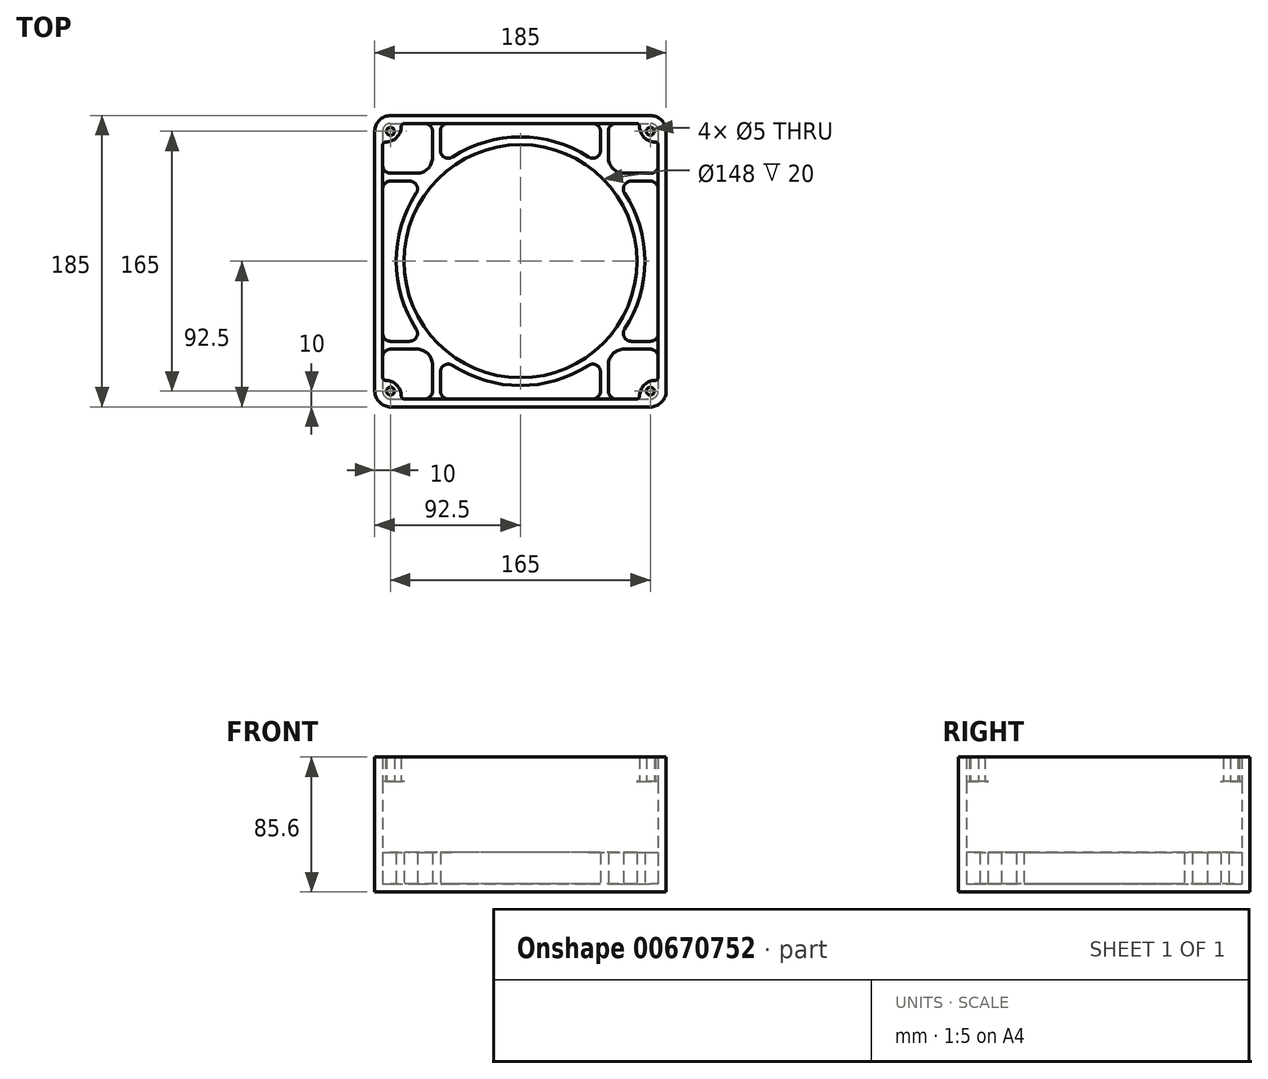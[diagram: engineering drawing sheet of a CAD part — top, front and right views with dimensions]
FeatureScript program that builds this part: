
annotation { "Feature Type Name" : "Feature", "Feature Type Description" : "" }
export const myFeature = defineFeature(function(context is Context, id is Id, definition is map)
    precondition{}
    {
        {
            var Q0;
            Q0=qCreatedBy(makeId("Top.planeOp"),FACE);
            var sketch = newSketch(context, id + "F0", { "sketchPlane" : qUnion([Q0])});
            skLineSegment(sketch, "E0.bottom", {"start": v(-82.5, 92.5) * mm, "end": v(82.5, 92.5) * mm});
            skLineSegment(sketch, "E0.top", {"start": v(-82.5, -92.5) * mm, "end": v(82.5, -92.5) * mm});
            skLineSegment(sketch, "E0.left", {"start": v(-92.5, 82.5) * mm, "end": v(-92.5, -82.5) * mm});
            skLineSegment(sketch, "E0.right", {"start": v(92.5, 82.5) * mm, "end": v(92.5, -82.5) * mm});
            skLineSegment(sketch, "E1", {"start": v(-92.5, 92.5) * mm, "end": v(92.5, -92.5) * mm, "construction": true});
            skLineSegment(sketch, "E2", {"start": v(-92.5, -92.5) * mm, "end": v(92.5, 92.5) * mm, "construction": true});
            skCircle(sketch, "E3", {"center": v(0, 0) * mm, "radius": 74 * mm});
            skArc(sketch, "E4.0", {"start": v(-66.19, 43.13) * mm, "mid": v(-79, 0) * mm, "end": v(-66.19, -43.13) * mm});
            skPoint(sketch, "E5.visualSharp", {"position": v(-92.5, 92.5) * mm});
            skArc(sketch, "E5.filletArc", {"start": v(-82.5, 92.5) * mm, "mid": v(-89.57, 89.57) * mm, "end": v(-92.5, 82.5) * mm});
            skPoint(sketch, "E6.visualSharp", {"position": v(92.5, 92.5) * mm});
            skArc(sketch, "E6.filletArc", {"start": v(92.5, 82.5) * mm, "mid": v(89.57, 89.57) * mm, "end": v(82.5, 92.5) * mm});
            skPoint(sketch, "E7.visualSharp", {"position": v(92.5, -92.5) * mm});
            skArc(sketch, "E7.filletArc", {"start": v(82.5, -92.5) * mm, "mid": v(89.57, -89.57) * mm, "end": v(92.5, -82.5) * mm});
            skPoint(sketch, "E8.visualSharp", {"position": v(-92.5, -92.5) * mm});
            skArc(sketch, "E8.filletArc", {"start": v(-92.5, -82.5) * mm, "mid": v(-89.57, -89.57) * mm, "end": v(-82.5, -92.5) * mm});
            skArc(sketch, "E9.0", {"start": v(-82.5, 87.5) * mm, "mid": v(-86.04, 86.04) * mm, "end": v(-87.5, 82.5) * mm});
            skLineSegment(sketch, "E9.1", {"start": v(-82.5, 87.5) * mm, "end": v(-60.86, 87.5) * mm});
            skLineSegment(sketch, "E9.2", {"start": v(-87.5, 82.5) * mm, "end": v(-87.5, 60.86) * mm});
            skArc(sketch, "E9.3", {"start": v(87.5, 82.5) * mm, "mid": v(86.04, 86.04) * mm, "end": v(82.5, 87.5) * mm});
            skArc(sketch, "E9.4", {"start": v(-87.5, -82.5) * mm, "mid": v(-86.04, -86.04) * mm, "end": v(-82.5, -87.5) * mm});
            skLineSegment(sketch, "E9.5", {"start": v(-82.5, -87.5) * mm, "end": v(-60.86, -87.5) * mm});
            skArc(sketch, "E9.6", {"start": v(82.5, -87.5) * mm, "mid": v(86.04, -86.04) * mm, "end": v(87.5, -82.5) * mm});
            skLineSegment(sketch, "E9.7", {"start": v(87.5, 82.5) * mm, "end": v(87.5, 60.86) * mm});
            skLineSegment(sketch, "E10", {"start": v(-55.86, 65.86) * mm, "end": v(-55.86, 82.5) * mm});
            skLineSegment(sketch, "E11", {"start": v(-65.86, 55.86) * mm, "end": v(-82.5, 55.86) * mm});
            skLineSegment(sketch, "E12", {"start": v(-50.86, 82.5) * mm, "end": v(-50.86, 70.38) * mm});
            skLineSegment(sketch, "E13", {"start": v(-82.5, 50.86) * mm, "end": v(-70.38, 50.86) * mm});
            skLineSegment(sketch, "E14", {"start": v(55.86, 65.86) * mm, "end": v(55.86, 82.5) * mm});
            skLineSegment(sketch, "E15", {"start": v(65.86, 55.86) * mm, "end": v(82.5, 55.86) * mm});
            skLineSegment(sketch, "E16", {"start": v(50.86, 82.5) * mm, "end": v(50.86, 70.38) * mm});
            skLineSegment(sketch, "E17", {"start": v(70.38, 50.86) * mm, "end": v(82.5, 50.86) * mm});
            skLineSegment(sketch, "E18", {"start": v(65.86, -55.86) * mm, "end": v(82.5, -55.86) * mm});
            skLineSegment(sketch, "E19", {"start": v(55.86, -65.86) * mm, "end": v(55.86, -82.5) * mm});
            skLineSegment(sketch, "E20", {"start": v(70.38, -50.86) * mm, "end": v(82.5, -50.86) * mm});
            skLineSegment(sketch, "E21", {"start": v(50.86, -70.38) * mm, "end": v(50.86, -82.5) * mm});
            skLineSegment(sketch, "E22", {"start": v(-55.86, -65.86) * mm, "end": v(-55.86, -82.5) * mm});
            skLineSegment(sketch, "E23", {"start": v(-65.86, -55.86) * mm, "end": v(-82.5, -55.86) * mm});
            skLineSegment(sketch, "E24", {"start": v(-50.86, -82.5) * mm, "end": v(-50.86, -70.38) * mm});
            skLineSegment(sketch, "E25", {"start": v(-82.5, -50.86) * mm, "end": v(-70.38, -50.86) * mm});
            skPoint(sketch, "E26.visualSharp", {"position": v(-55.86, 55.86) * mm});
            skArc(sketch, "E26.filletArc", {"start": v(-65.86, 55.86) * mm, "mid": v(-58.8, 58.8) * mm, "end": v(-55.86, 65.86) * mm});
            skPoint(sketch, "E27.visualSharp", {"position": v(55.86, 55.86) * mm});
            skArc(sketch, "E27.filletArc", {"start": v(55.86, 65.86) * mm, "mid": v(58.8, 58.8) * mm, "end": v(65.86, 55.86) * mm});
            skPoint(sketch, "E28.visualSharp", {"position": v(55.86, -55.86) * mm});
            skArc(sketch, "E28.filletArc", {"start": v(65.86, -55.86) * mm, "mid": v(58.8, -58.8) * mm, "end": v(55.86, -65.86) * mm});
            skPoint(sketch, "E29.visualSharp", {"position": v(-55.86, -55.86) * mm});
            skArc(sketch, "E29.filletArc", {"start": v(-55.86, -65.86) * mm, "mid": v(-58.8, -58.8) * mm, "end": v(-65.86, -55.86) * mm});
            skLineSegment(sketch, "E30.trimOffspring", {"start": v(-87.5, 45.86) * mm, "end": v(-87.5, -45.86) * mm});
            skLineSegment(sketch, "E31.trimOffspring", {"start": v(-45.86, 87.5) * mm, "end": v(45.86, 87.5) * mm});
            skArc(sketch, "E32.trimOffspring", {"start": v(43.13, 66.19) * mm, "mid": v(0, 79) * mm, "end": v(-43.13, 66.19) * mm});
            skLineSegment(sketch, "E33.trimOffspring", {"start": v(60.86, 87.5) * mm, "end": v(82.5, 87.5) * mm});
            skLineSegment(sketch, "E34.trimOffspring", {"start": v(87.5, 45.86) * mm, "end": v(87.5, -45.86) * mm});
            skLineSegment(sketch, "E35.trimOffspring", {"start": v(87.5, -60.86) * mm, "end": v(87.5, -82.5) * mm});
            skArc(sketch, "E36.trimOffspring", {"start": v(66.19, -43.13) * mm, "mid": v(79, 0) * mm, "end": v(66.19, 43.13) * mm});
            skLineSegment(sketch, "E37.trimOffspring", {"start": v(60.86, -87.5) * mm, "end": v(82.5, -87.5) * mm});
            skLineSegment(sketch, "E38.trimOffspring", {"start": v(-45.86, -87.5) * mm, "end": v(45.86, -87.5) * mm});
            skLineSegment(sketch, "E39.trimOffspring", {"start": v(-87.5, -60.86) * mm, "end": v(-87.5, -82.5) * mm});
            skArc(sketch, "E40.trimOffspring", {"start": v(-43.13, -66.19) * mm, "mid": v(0, -79) * mm, "end": v(43.13, -66.19) * mm});
            skPoint(sketch, "E41.visualSharp", {"position": v(-55.86, 87.5) * mm});
            skArc(sketch, "E41.filletArc", {"start": v(-55.86, 82.5) * mm, "mid": v(-57.33, 86.04) * mm, "end": v(-60.86, 87.5) * mm});
            skPoint(sketch, "E42.visualSharp", {"position": v(-50.86, 87.5) * mm});
            skArc(sketch, "E42.filletArc", {"start": v(-45.86, 87.5) * mm, "mid": v(-49.4, 86.04) * mm, "end": v(-50.86, 82.5) * mm});
            skPoint(sketch, "E43.visualSharp", {"position": v(-50.86, 60.45) * mm});
            skArc(sketch, "E43.filletArc", {"start": v(-50.86, 70.38) * mm, "mid": v(-48.24, 65.98) * mm, "end": v(-43.13, 66.19) * mm});
            skPoint(sketch, "E44.visualSharp", {"position": v(-60.45, 50.86) * mm});
            skArc(sketch, "E44.filletArc", {"start": v(-66.19, 43.13) * mm, "mid": v(-65.98, 48.24) * mm, "end": v(-70.38, 50.86) * mm});
            skPoint(sketch, "E45.visualSharp", {"position": v(-87.5, 50.86) * mm});
            skArc(sketch, "E45.filletArc", {"start": v(-82.5, 50.86) * mm, "mid": v(-86.04, 49.4) * mm, "end": v(-87.5, 45.86) * mm});
            skPoint(sketch, "E46.visualSharp", {"position": v(-87.5, 55.86) * mm});
            skArc(sketch, "E46.filletArc", {"start": v(-87.5, 60.86) * mm, "mid": v(-86.04, 57.33) * mm, "end": v(-82.5, 55.86) * mm});
            skPoint(sketch, "E47.visualSharp", {"position": v(55.86, 87.5) * mm});
            skArc(sketch, "E47.filletArc", {"start": v(60.86, 87.5) * mm, "mid": v(57.33, 86.04) * mm, "end": v(55.86, 82.5) * mm});
            skPoint(sketch, "E48.visualSharp", {"position": v(50.86, 87.5) * mm});
            skArc(sketch, "E48.filletArc", {"start": v(50.86, 82.5) * mm, "mid": v(49.4, 86.04) * mm, "end": v(45.86, 87.5) * mm});
            skPoint(sketch, "E49.visualSharp", {"position": v(50.86, 60.45) * mm});
            skArc(sketch, "E49.filletArc", {"start": v(43.13, 66.19) * mm, "mid": v(48.24, 65.98) * mm, "end": v(50.86, 70.38) * mm});
            skPoint(sketch, "E50.visualSharp", {"position": v(60.45, 50.86) * mm});
            skArc(sketch, "E50.filletArc", {"start": v(70.38, 50.86) * mm, "mid": v(65.98, 48.24) * mm, "end": v(66.19, 43.13) * mm});
            skPoint(sketch, "E51.visualSharp", {"position": v(87.5, 55.86) * mm});
            skArc(sketch, "E51.filletArc", {"start": v(82.5, 55.86) * mm, "mid": v(86.04, 57.33) * mm, "end": v(87.5, 60.86) * mm});
            skPoint(sketch, "E52.visualSharp", {"position": v(87.5, 50.86) * mm});
            skArc(sketch, "E52.filletArc", {"start": v(87.5, 45.86) * mm, "mid": v(86.04, 49.4) * mm, "end": v(82.5, 50.86) * mm});
            skPoint(sketch, "E53.visualSharp", {"position": v(87.5, -50.86) * mm});
            skArc(sketch, "E53.filletArc", {"start": v(82.5, -50.86) * mm, "mid": v(86.04, -49.4) * mm, "end": v(87.5, -45.86) * mm});
            skPoint(sketch, "E54.visualSharp", {"position": v(87.5, -55.86) * mm});
            skArc(sketch, "E54.filletArc", {"start": v(87.5, -60.86) * mm, "mid": v(86.04, -57.33) * mm, "end": v(82.5, -55.86) * mm});
            skPoint(sketch, "E55.visualSharp", {"position": v(60.45, -50.86) * mm});
            skArc(sketch, "E55.filletArc", {"start": v(66.19, -43.13) * mm, "mid": v(65.98, -48.24) * mm, "end": v(70.38, -50.86) * mm});
            skPoint(sketch, "E56.visualSharp", {"position": v(50.86, -60.45) * mm});
            skArc(sketch, "E56.filletArc", {"start": v(50.86, -70.38) * mm, "mid": v(48.24, -65.98) * mm, "end": v(43.13, -66.19) * mm});
            skPoint(sketch, "E57.visualSharp", {"position": v(55.86, -87.5) * mm});
            skArc(sketch, "E57.filletArc", {"start": v(55.86, -82.5) * mm, "mid": v(57.33, -86.04) * mm, "end": v(60.86, -87.5) * mm});
            skPoint(sketch, "E58.visualSharp", {"position": v(50.86, -87.5) * mm});
            skArc(sketch, "E58.filletArc", {"start": v(45.86, -87.5) * mm, "mid": v(49.4, -86.04) * mm, "end": v(50.86, -82.5) * mm});
            skPoint(sketch, "E59.visualSharp", {"position": v(-55.86, -87.5) * mm});
            skArc(sketch, "E59.filletArc", {"start": v(-60.86, -87.5) * mm, "mid": v(-57.33, -86.04) * mm, "end": v(-55.86, -82.5) * mm});
            skPoint(sketch, "E60.visualSharp", {"position": v(-50.86, -87.5) * mm});
            skArc(sketch, "E60.filletArc", {"start": v(-50.86, -82.5) * mm, "mid": v(-49.4, -86.04) * mm, "end": v(-45.86, -87.5) * mm});
            skPoint(sketch, "E61.visualSharp", {"position": v(-50.86, -60.45) * mm});
            skArc(sketch, "E61.filletArc", {"start": v(-43.13, -66.19) * mm, "mid": v(-48.24, -65.98) * mm, "end": v(-50.86, -70.38) * mm});
            skPoint(sketch, "E62.visualSharp", {"position": v(-60.45, -50.86) * mm});
            skArc(sketch, "E62.filletArc", {"start": v(-70.38, -50.86) * mm, "mid": v(-65.98, -48.24) * mm, "end": v(-66.19, -43.13) * mm});
            skPoint(sketch, "E63.visualSharp", {"position": v(-87.5, -50.86) * mm});
            skArc(sketch, "E63.filletArc", {"start": v(-87.5, -45.86) * mm, "mid": v(-86.04, -49.4) * mm, "end": v(-82.5, -50.86) * mm});
            skPoint(sketch, "E64.visualSharp", {"position": v(-87.5, -55.86) * mm});
            skArc(sketch, "E64.filletArc", {"start": v(-82.5, -55.86) * mm, "mid": v(-86.04, -57.33) * mm, "end": v(-87.5, -60.86) * mm});
            skSolve(sketch);
        }
        {
            var Q0;
            Q0=makeQuery(id+"F0.imprint","IMPRINT",FACE,{"disambiguationData":[TD([[makeQuery(id+"F0.imprint","IMPRINT",EDGE,{"derivedFrom":sQuery(id+"F0.wireOp",EDGE,"E0.bottom")}),-1.0]])]});
            var Q1;
            Q1=makeQuery(id+"F0.imprint","IMPRINT",FACE,{"disambiguationData":[TD([[makeQuery(id+"F0.imprint","IMPRINT",EDGE,{"derivedFrom":sQuery(id+"F0.wireOp",EDGE,"E3")}),1.0]])]});
            var Q2;
            Q2=makeQuery(id+"F0.imprint","IMPRINT",FACE,{"disambiguationData":[TD([[makeQuery(id+"F0.imprint","IMPRINT",EDGE,{"derivedFrom":sQuery(id+"F0.wireOp",EDGE,"E3")}),-1.0]])]});
            var Q3;
            {var subQ5=sQuery(id+"F0.wireOp",EDGE,"E9.0");Q3=makeQuery(id+"F0.imprint","IMPRINT",FACE,{"disambiguationData":[TD([[makeQuery(id+"F0.imprint","IMPRINT",EDGE,{"derivedFrom":subQ5}),1.0]])]});}
            var Q4;
            {var subQ5=sQuery(id+"F0.wireOp",EDGE,"E9.4");Q4=makeQuery(id+"F0.imprint","IMPRINT",FACE,{"disambiguationData":[TD([[makeQuery(id+"F0.imprint","IMPRINT",EDGE,{"derivedFrom":subQ5}),1.0]])]});}
            var Q5;
            {var subQ5=sQuery(id+"F0.wireOp",EDGE,"E9.6");Q5=makeQuery(id+"F0.imprint","IMPRINT",FACE,{"disambiguationData":[TD([[makeQuery(id+"F0.imprint","IMPRINT",EDGE,{"derivedFrom":subQ5}),1.0]])]});}
            var Q6;
            {var subQ5=sQuery(id+"F0.wireOp",EDGE,"E9.3");Q6=makeQuery(id+"F0.imprint","IMPRINT",FACE,{"disambiguationData":[TD([[makeQuery(id+"F0.imprint","IMPRINT",EDGE,{"derivedFrom":subQ5}),1.0]])]});}
            var Q7;
            Q7=makeQuery(id+"F0.imprint","IMPRINT",FACE,{"disambiguationData":[TD([[makeQuery(id+"F0.imprint","IMPRINT",EDGE,{"derivedFrom":sQuery(id+"F0.wireOp",EDGE,"E4.0")}),-1.0]])]});
            var Q8;
            Q8=makeQuery(id+"F0.imprint","IMPRINT",FACE,{"disambiguationData":[TD([[makeQuery(id+"F0.imprint","IMPRINT",EDGE,{"derivedFrom":sQuery(id+"F0.wireOp",EDGE,"E12")}),1.0]])]});
            var Q9;
            Q9=makeQuery(id+"F0.imprint","IMPRINT",FACE,{"disambiguationData":[TD([[makeQuery(id+"F0.imprint","IMPRINT",EDGE,{"derivedFrom":sQuery(id+"F0.wireOp",EDGE,"E21")}),-1.0]])]});
            var Q10;
            Q10=makeQuery(id+"F0.imprint","IMPRINT",FACE,{"disambiguationData":[TD([[makeQuery(id+"F0.imprint","IMPRINT",EDGE,{"derivedFrom":sQuery(id+"F0.wireOp",EDGE,"E17")}),-1.0]])]});
            extrude(context, id + "F1", {"entities" : qUnion([Q0, Q1, Q2, Q3, Q4, Q5, Q6, Q7, Q8, Q9, Q10]), "oppositeDirection" : true, "depth" : 5 * mm, "offsetDistance" : 25 * mm});
        }
        {
            var Q0;
            Q0 = qSketchRegion(id + "F0", true);
            extrude(context, id + "F2", {"entities" : qUnion([Q0]), "operationType" : NewBodyOperationType.ADD, "depth" : 20 * mm, "offsetDistance" : 25 * mm});
        }
        {
            var Q0;
            Q0=makeQuery(id+"F2.opExtrude","CAP_FACE",FACE,{"disambiguationData":[OSD([sQuery(id+"F0.wireOp",EDGE,"E0.bottom"),sQuery(id+"F0.wireOp",EDGE,"E0.top"),sQuery(id+"F0.wireOp",EDGE,"E0.left"),sQuery(id+"F0.wireOp",EDGE,"E0.right"),sQuery(id+"F0.wireOp",EDGE,"E3"),sQuery(id+"F0.wireOp",EDGE,"E4.0"),sQuery(id+"F0.wireOp",EDGE,"E5.filletArc"),sQuery(id+"F0.wireOp",EDGE,"E6.filletArc"),sQuery(id+"F0.wireOp",EDGE,"E7.filletArc"),sQuery(id+"F0.wireOp",EDGE,"E8.filletArc"),sQuery(id+"F0.wireOp",EDGE,"E9.0"),sQuery(id+"F0.wireOp",EDGE,"E9.1"),sQuery(id+"F0.wireOp",EDGE,"E9.2"),sQuery(id+"F0.wireOp",EDGE,"E9.3"),sQuery(id+"F0.wireOp",EDGE,"E9.4"),sQuery(id+"F0.wireOp",EDGE,"E9.5"),sQuery(id+"F0.wireOp",EDGE,"E9.6"),sQuery(id+"F0.wireOp",EDGE,"E9.7"),sQuery(id+"F0.wireOp",EDGE,"E10"),sQuery(id+"F0.wireOp",EDGE,"E11"),sQuery(id+"F0.wireOp",EDGE,"E12"),sQuery(id+"F0.wireOp",EDGE,"E13"),sQuery(id+"F0.wireOp",EDGE,"E14"),sQuery(id+"F0.wireOp",EDGE,"E15"),sQuery(id+"F0.wireOp",EDGE,"E16"),sQuery(id+"F0.wireOp",EDGE,"E17"),sQuery(id+"F0.wireOp",EDGE,"E18"),sQuery(id+"F0.wireOp",EDGE,"E19"),sQuery(id+"F0.wireOp",EDGE,"E20"),sQuery(id+"F0.wireOp",EDGE,"E21"),sQuery(id+"F0.wireOp",EDGE,"E22"),sQuery(id+"F0.wireOp",EDGE,"E23"),sQuery(id+"F0.wireOp",EDGE,"E24"),sQuery(id+"F0.wireOp",EDGE,"E25"),sQuery(id+"F0.wireOp",EDGE,"E26.filletArc"),sQuery(id+"F0.wireOp",EDGE,"E27.filletArc"),sQuery(id+"F0.wireOp",EDGE,"E28.filletArc"),sQuery(id+"F0.wireOp",EDGE,"E29.filletArc"),sQuery(id+"F0.wireOp",EDGE,"E30.trimOffspring"),sQuery(id+"F0.wireOp",EDGE,"E31.trimOffspring"),sQuery(id+"F0.wireOp",EDGE,"E32.trimOffspring"),sQuery(id+"F0.wireOp",EDGE,"E33.trimOffspring"),sQuery(id+"F0.wireOp",EDGE,"E34.trimOffspring"),sQuery(id+"F0.wireOp",EDGE,"E35.trimOffspring"),sQuery(id+"F0.wireOp",EDGE,"E36.trimOffspring"),sQuery(id+"F0.wireOp",EDGE,"E37.trimOffspring"),sQuery(id+"F0.wireOp",EDGE,"E38.trimOffspring"),sQuery(id+"F0.wireOp",EDGE,"E39.trimOffspring"),sQuery(id+"F0.wireOp",EDGE,"E40.trimOffspring"),sQuery(id+"F0.wireOp",EDGE,"E41.filletArc"),sQuery(id+"F0.wireOp",EDGE,"E42.filletArc"),sQuery(id+"F0.wireOp",EDGE,"E43.filletArc"),sQuery(id+"F0.wireOp",EDGE,"E44.filletArc"),sQuery(id+"F0.wireOp",EDGE,"E45.filletArc"),sQuery(id+"F0.wireOp",EDGE,"E46.filletArc"),sQuery(id+"F0.wireOp",EDGE,"E47.filletArc"),sQuery(id+"F0.wireOp",EDGE,"E48.filletArc"),sQuery(id+"F0.wireOp",EDGE,"E49.filletArc"),sQuery(id+"F0.wireOp",EDGE,"E50.filletArc"),sQuery(id+"F0.wireOp",EDGE,"E51.filletArc"),sQuery(id+"F0.wireOp",EDGE,"E52.filletArc"),sQuery(id+"F0.wireOp",EDGE,"E53.filletArc"),sQuery(id+"F0.wireOp",EDGE,"E54.filletArc"),sQuery(id+"F0.wireOp",EDGE,"E55.filletArc"),sQuery(id+"F0.wireOp",EDGE,"E56.filletArc"),sQuery(id+"F0.wireOp",EDGE,"E57.filletArc"),sQuery(id+"F0.wireOp",EDGE,"E58.filletArc"),sQuery(id+"F0.wireOp",EDGE,"E59.filletArc"),sQuery(id+"F0.wireOp",EDGE,"E60.filletArc"),sQuery(id+"F0.wireOp",EDGE,"E61.filletArc"),sQuery(id+"F0.wireOp",EDGE,"E62.filletArc"),sQuery(id+"F0.wireOp",EDGE,"E63.filletArc"),sQuery(id+"F0.wireOp",EDGE,"E64.filletArc")])],"isStart":false});
            var sketch = newSketch(context, id + "F3", { "sketchPlane" : qUnion([Q0])});
            skLineSegment(sketch, "E65.0", {"start": v(-92.5, 82.5) * mm, "end": v(-92.5, -82.5) * mm});
            skArc(sketch, "E65.1", {"start": v(-82.5, 92.5) * mm, "mid": v(-89.57, 89.57) * mm, "end": v(-92.5, 82.5) * mm});
            skLineSegment(sketch, "E65.2", {"start": v(-82.5, 92.5) * mm, "end": v(82.5, 92.5) * mm});
            skArc(sketch, "E65.3", {"start": v(92.5, 82.5) * mm, "mid": v(89.57, 89.57) * mm, "end": v(82.5, 92.5) * mm});
            skLineSegment(sketch, "E65.4", {"start": v(92.5, 82.5) * mm, "end": v(92.5, -82.5) * mm});
            skArc(sketch, "E65.5", {"start": v(82.5, -92.5) * mm, "mid": v(89.57, -89.57) * mm, "end": v(92.5, -82.5) * mm});
            skLineSegment(sketch, "E65.6", {"start": v(-82.5, -92.5) * mm, "end": v(82.5, -92.5) * mm});
            skArc(sketch, "E65.7", {"start": v(-92.5, -82.5) * mm, "mid": v(-89.57, -89.57) * mm, "end": v(-82.5, -92.5) * mm});
            skArc(sketch, "E66.0", {"start": v(-82.5, 87.5) * mm, "mid": v(-86.04, 86.04) * mm, "end": v(-87.5, 82.5) * mm});
            skLineSegment(sketch, "E66.1", {"start": v(-82.5, 87.5) * mm, "end": v(82.5, 87.5) * mm});
            skLineSegment(sketch, "E66.2", {"start": v(-87.5, 82.5) * mm, "end": v(-87.5, -82.5) * mm});
            skArc(sketch, "E66.3", {"start": v(87.5, 82.5) * mm, "mid": v(86.04, 86.04) * mm, "end": v(82.5, 87.5) * mm});
            skArc(sketch, "E66.4", {"start": v(-87.5, -82.5) * mm, "mid": v(-86.04, -86.04) * mm, "end": v(-82.5, -87.5) * mm});
            skLineSegment(sketch, "E66.5", {"start": v(-82.5, -87.5) * mm, "end": v(82.5, -87.5) * mm});
            skArc(sketch, "E66.6", {"start": v(82.5, -87.5) * mm, "mid": v(86.04, -86.04) * mm, "end": v(87.5, -82.5) * mm});
            skLineSegment(sketch, "E66.7", {"start": v(87.5, 82.5) * mm, "end": v(87.5, -82.5) * mm});
            skSolve(sketch);
        }
        {
            var Q0;
            Q0 = qSketchRegion(id + "F3", true);
            extrude(context, id + "F4", {"entities" : qUnion([Q0]), "operationType" : NewBodyOperationType.ADD, "depth" : (65.1 - 20) * mm, "offsetDistance" : 25 * mm});
        }
        {
            var Q0;
            Q0=makeQuery(id+"F4.opExtrude","CAP_FACE",FACE,{"disambiguationData":[OSD([sQuery(id+"F3.wireOp",EDGE,"E65.0"),sQuery(id+"F3.wireOp",EDGE,"E65.1"),sQuery(id+"F3.wireOp",EDGE,"E65.2"),sQuery(id+"F3.wireOp",EDGE,"E65.3"),sQuery(id+"F3.wireOp",EDGE,"E65.4"),sQuery(id+"F3.wireOp",EDGE,"E65.5"),sQuery(id+"F3.wireOp",EDGE,"E65.6"),sQuery(id+"F3.wireOp",EDGE,"E65.7"),sQuery(id+"F3.wireOp",EDGE,"E66.0"),sQuery(id+"F3.wireOp",EDGE,"E66.1"),sQuery(id+"F3.wireOp",EDGE,"E66.2"),sQuery(id+"F3.wireOp",EDGE,"E66.3"),sQuery(id+"F3.wireOp",EDGE,"E66.4"),sQuery(id+"F3.wireOp",EDGE,"E66.5"),sQuery(id+"F3.wireOp",EDGE,"E66.6"),sQuery(id+"F3.wireOp",EDGE,"E66.7")])],"isStart":false});
            var sketch = newSketch(context, id + "F5", { "sketchPlane" : qUnion([Q0])});
            skArc(sketch, "E67.0", {"start": v(-82.5, 92.5) * mm, "mid": v(-89.57, 89.57) * mm, "end": v(-92.5, 82.5) * mm});
            skLineSegment(sketch, "E67.1", {"start": v(-82.5, 92.5) * mm, "end": v(82.5, 92.5) * mm});
            skLineSegment(sketch, "E67.2", {"start": v(-92.5, 82.5) * mm, "end": v(-92.5, -82.5) * mm});
            skArc(sketch, "E67.3", {"start": v(-92.5, -82.5) * mm, "mid": v(-89.57, -89.57) * mm, "end": v(-82.5, -92.5) * mm});
            skLineSegment(sketch, "E67.4", {"start": v(-82.5, -92.5) * mm, "end": v(82.5, -92.5) * mm});
            skArc(sketch, "E67.5", {"start": v(82.5, -92.5) * mm, "mid": v(89.57, -89.57) * mm, "end": v(92.5, -82.5) * mm});
            skLineSegment(sketch, "E67.6", {"start": v(92.5, 82.5) * mm, "end": v(92.5, -82.5) * mm});
            skArc(sketch, "E67.7", {"start": v(92.5, 82.5) * mm, "mid": v(89.57, 89.57) * mm, "end": v(82.5, 92.5) * mm});
            skLineSegment(sketch, "E68.1", {"start": v(-73.68, 87.5) * mm, "end": v(-60.86, 87.5) * mm});
            skLineSegment(sketch, "E68.2", {"start": v(-87.5, 73.68) * mm, "end": v(-87.5, 60.86) * mm});
            skLineSegment(sketch, "E68.5", {"start": v(-73.68, -87.5) * mm, "end": v(-60.86, -87.5) * mm});
            skLineSegment(sketch, "E68.7", {"start": v(87.5, 73.68) * mm, "end": v(87.5, 60.86) * mm});
            skLineSegment(sketch, "E69.trimOffspring", {"start": v(-45.86, 87.5) * mm, "end": v(45.86, 87.5) * mm});
            skLineSegment(sketch, "E70.trimOffspring", {"start": v(-87.5, 45.86) * mm, "end": v(-87.5, -45.86) * mm});
            skLineSegment(sketch, "E71.trimOffspring", {"start": v(60.86, 87.5) * mm, "end": v(73.68, 87.5) * mm});
            skLineSegment(sketch, "E72.trimOffspring", {"start": v(87.5, 45.86) * mm, "end": v(87.5, -45.86) * mm});
            skLineSegment(sketch, "E73.trimOffspring", {"start": v(87.5, -60.86) * mm, "end": v(87.5, -73.68) * mm});
            skLineSegment(sketch, "E74.trimOffspring", {"start": v(60.86, -87.5) * mm, "end": v(73.68, -87.5) * mm});
            skLineSegment(sketch, "E75.trimOffspring", {"start": v(-45.86, -87.5) * mm, "end": v(45.86, -87.5) * mm});
            skLineSegment(sketch, "E76.trimOffspring", {"start": v(-87.5, -60.86) * mm, "end": v(-87.5, -73.68) * mm});
            skLineSegment(sketch, "E77", {"start": v(75.68, 75.68) * mm, "end": v(89.57, 89.57) * mm, "construction": true});
            skLineSegment(sketch, "E78", {"start": v(75.68, -75.68) * mm, "end": v(89.57, -89.57) * mm, "construction": true});
            skLineSegment(sketch, "E79", {"start": v(-75.68, -75.68) * mm, "end": v(-89.57, -89.57) * mm, "construction": true});
            skLineSegment(sketch, "E80", {"start": v(-75.68, 75.68) * mm, "end": v(-89.57, 89.57) * mm, "construction": true});
            skCircle(sketch, "E81", {"center": v(-82.5, 82.5) * mm, "radius": 2.5 * mm});
            skCircle(sketch, "E82", {"center": v(82.5, 82.5) * mm, "radius": 2.5 * mm});
            skCircle(sketch, "E83", {"center": v(82.5, -82.5) * mm, "radius": 2.5 * mm});
            skCircle(sketch, "E84", {"center": v(-82.5, -82.5) * mm, "radius": 2.5 * mm});
            skLineSegment(sketch, "E85", {"start": v(-75.68, 85.5) * mm, "end": v(-75.68, 85.68) * mm});
            skLineSegment(sketch, "E86", {"start": v(-85.5, 75.68) * mm, "end": v(-85.68, 75.68) * mm});
            skLineSegment(sketch, "E87", {"start": v(75.68, 85.5) * mm, "end": v(75.68, 85.68) * mm});
            skLineSegment(sketch, "E88", {"start": v(85.5, 75.68) * mm, "end": v(85.68, 75.68) * mm});
            skLineSegment(sketch, "E89", {"start": v(85.5, -75.68) * mm, "end": v(85.68, -75.68) * mm});
            skLineSegment(sketch, "E90", {"start": v(75.68, -85.5) * mm, "end": v(75.68, -85.68) * mm});
            skLineSegment(sketch, "E91", {"start": v(-75.68, -85.5) * mm, "end": v(-75.68, -85.68) * mm});
            skLineSegment(sketch, "E92", {"start": v(-85.5, -75.68) * mm, "end": v(-85.68, -75.68) * mm});
            skPoint(sketch, "E93.orphan", {"position": v(-87.5, -63.86) * mm});
            skPoint(sketch, "E94.end.orphan", {"position": v(-63.86, -87.5) * mm});
            skPoint(sketch, "E95.orphan", {"position": v(87.5, -82.5) * mm});
            skPoint(sketch, "E96.start.orphan", {"position": v(84.37, -84.37) * mm});
            skPoint(sketch, "E97.orphan", {"position": v(63.86, 87.5) * mm});
            skPoint(sketch, "E98.end.orphan", {"position": v(87.5, 63.86) * mm});
            skPoint(sketch, "E99.orphan", {"position": v(-63.86, 87.5) * mm});
            skPoint(sketch, "E100.start.orphan", {"position": v(-87.5, 63.86) * mm});
            skPoint(sketch, "E101.visualSharp", {"position": v(-75.68, 75.68) * mm});
            skArc(sketch, "E101.filletArc", {"start": v(-85.68, 75.68) * mm, "mid": v(-78.61, 78.61) * mm, "end": v(-75.68, 85.68) * mm});
            skPoint(sketch, "E102.visualSharp", {"position": v(75.68, 75.68) * mm});
            skArc(sketch, "E102.filletArc", {"start": v(75.68, 85.68) * mm, "mid": v(78.61, 78.61) * mm, "end": v(85.68, 75.68) * mm});
            skPoint(sketch, "E103.visualSharp", {"position": v(75.68, -75.68) * mm});
            skArc(sketch, "E103.filletArc", {"start": v(85.68, -75.68) * mm, "mid": v(78.61, -78.61) * mm, "end": v(75.68, -85.68) * mm});
            skPoint(sketch, "E104.visualSharp", {"position": v(-75.68, -75.68) * mm});
            skArc(sketch, "E104.filletArc", {"start": v(-75.68, -85.68) * mm, "mid": v(-78.61, -78.61) * mm, "end": v(-85.68, -75.68) * mm});
            skPoint(sketch, "E105.orphan", {"position": v(-66.87, -87.5) * mm});
            skPoint(sketch, "E106.orphan", {"position": v(-87.5, -66.87) * mm});
            skPoint(sketch, "E107.orphan", {"position": v(87.5, -87.5) * mm});
            skPoint(sketch, "E108.orphan", {"position": v(87.5, -104.14) * mm});
            skPoint(sketch, "E109.orphan", {"position": v(66.87, 87.5) * mm});
            skPoint(sketch, "E110.orphan", {"position": v(87.5, 66.87) * mm});
            skPoint(sketch, "E111.orphan", {"position": v(-66.87, 87.5) * mm});
            skPoint(sketch, "E112.orphan", {"position": v(-87.5, 66.87) * mm});
            skPoint(sketch, "E113.visualSharp", {"position": v(-75.68, 87.5) * mm});
            skArc(sketch, "E113.filletArc", {"start": v(-73.68, 87.5) * mm, "mid": v(-75.1, 86.91) * mm, "end": v(-75.68, 85.5) * mm});
            skPoint(sketch, "E114.visualSharp", {"position": v(-87.5, 75.68) * mm});
            skArc(sketch, "E114.filletArc", {"start": v(-85.5, 75.68) * mm, "mid": v(-86.91, 75.1) * mm, "end": v(-87.5, 73.68) * mm});
            skPoint(sketch, "E115.visualSharp", {"position": v(75.68, 87.5) * mm});
            skArc(sketch, "E115.filletArc", {"start": v(75.68, 85.5) * mm, "mid": v(75.1, 86.91) * mm, "end": v(73.68, 87.5) * mm});
            skPoint(sketch, "E116.visualSharp", {"position": v(87.5, 75.68) * mm});
            skArc(sketch, "E116.filletArc", {"start": v(87.5, 73.68) * mm, "mid": v(86.91, 75.1) * mm, "end": v(85.5, 75.68) * mm});
            skPoint(sketch, "E117.visualSharp", {"position": v(87.5, -75.68) * mm});
            skArc(sketch, "E117.filletArc", {"start": v(85.5, -75.68) * mm, "mid": v(86.91, -75.1) * mm, "end": v(87.5, -73.68) * mm});
            skPoint(sketch, "E118.visualSharp", {"position": v(75.68, -87.5) * mm});
            skArc(sketch, "E118.filletArc", {"start": v(73.68, -87.5) * mm, "mid": v(75.1, -86.91) * mm, "end": v(75.68, -85.5) * mm});
            skPoint(sketch, "E119.visualSharp", {"position": v(-75.68, -87.5) * mm});
            skArc(sketch, "E119.filletArc", {"start": v(-75.68, -85.5) * mm, "mid": v(-75.1, -86.91) * mm, "end": v(-73.68, -87.5) * mm});
            skPoint(sketch, "E120.visualSharp", {"position": v(-87.5, -75.68) * mm});
            skArc(sketch, "E120.filletArc", {"start": v(-87.5, -73.68) * mm, "mid": v(-86.91, -75.1) * mm, "end": v(-85.5, -75.68) * mm});
            skLineSegment(sketch, "E121", {"start": v(-87.5, 60.86) * mm, "end": v(-87.5, 45.86) * mm});
            skLineSegment(sketch, "E122", {"start": v(-60.86, 87.5) * mm, "end": v(-45.86, 87.5) * mm});
            skLineSegment(sketch, "E123", {"start": v(45.86, 87.5) * mm, "end": v(60.86, 87.5) * mm});
            skLineSegment(sketch, "E124", {"start": v(87.5, 60.86) * mm, "end": v(87.5, 45.86) * mm});
            skLineSegment(sketch, "E125", {"start": v(87.5, -45.86) * mm, "end": v(87.5, -60.86) * mm});
            skLineSegment(sketch, "E126", {"start": v(60.86, -87.5) * mm, "end": v(45.86, -87.5) * mm});
            skLineSegment(sketch, "E127", {"start": v(-60.86, -87.5) * mm, "end": v(-45.86, -87.5) * mm});
            skLineSegment(sketch, "E128", {"start": v(-87.5, -60.86) * mm, "end": v(-87.5, -45.86) * mm});
            skPoint(sketch, "E129.4.end.orphan", {"position": v(-82.5, 55.86) * mm});
            skPoint(sketch, "E129.5.start.orphan", {"position": v(-82.5, 50.86) * mm});
            skPoint(sketch, "E129.2.start.orphan", {"position": v(-65.86, 55.86) * mm});
            skPoint(sketch, "E129.1.start.orphan", {"position": v(-55.86, 65.86) * mm});
            skPoint(sketch, "E129.0.start.orphan", {"position": v(-55.86, 82.5) * mm});
            skPoint(sketch, "E129.10.start.orphan", {"position": v(-50.86, 82.5) * mm});
            skPoint(sketch, "E129.11.start.orphan", {"position": v(-50.86, 70.38) * mm});
            skPoint(sketch, "E129.12.end.orphan", {"position": v(-43.13, 66.19) * mm});
            skPoint(sketch, "E129.13.start.orphan", {"position": v(43.13, 66.19) * mm});
            skPoint(sketch, "E129.14.end.orphan", {"position": v(50.86, 70.38) * mm});
            skPoint(sketch, "E129.15.start.orphan", {"position": v(50.86, 82.5) * mm});
            skPoint(sketch, "E129.17.end.orphan", {"position": v(55.86, 82.5) * mm});
            skPoint(sketch, "E129.18.start.orphan", {"position": v(55.86, 65.86) * mm});
            skPoint(sketch, "E129.19.start.orphan", {"position": v(65.86, 55.86) * mm});
            skPoint(sketch, "E129.20.start.orphan", {"position": v(82.5, 55.86) * mm});
            skPoint(sketch, "E129.22.end.orphan", {"position": v(82.5, 50.86) * mm});
            skPoint(sketch, "E129.23.start.orphan", {"position": v(70.38, 50.86) * mm});
            skPoint(sketch, "E129.24.end.orphan", {"position": v(66.19, 43.13) * mm});
            skPoint(sketch, "E129.7.end.orphan", {"position": v(-70.38, 50.86) * mm});
            skPoint(sketch, "E129.8.start.orphan", {"position": v(-66.19, 43.13) * mm});
            skPoint(sketch, "E129.26.start.orphan", {"position": v(66.19, -43.13) * mm});
            skPoint(sketch, "E129.27.start.orphan", {"position": v(70.38, -50.86) * mm});
            skPoint(sketch, "E129.28.start.orphan", {"position": v(82.5, -50.86) * mm});
            skPoint(sketch, "E129.30.end.orphan", {"position": v(82.5, -55.86) * mm});
            skPoint(sketch, "E129.31.start.orphan", {"position": v(65.86, -55.86) * mm});
            skPoint(sketch, "E129.34.start.orphan", {"position": v(55.86, -65.86) * mm});
            skPoint(sketch, "E129.35.start.orphan", {"position": v(55.86, -82.5) * mm});
            skPoint(sketch, "E129.33.end.orphan", {"position": v(50.86, -82.5) * mm});
            skPoint(sketch, "E129.32.start.orphan", {"position": v(50.86, -70.38) * mm});
            skPoint(sketch, "E129.37.end.orphan", {"position": v(43.13, -66.19) * mm});
            skPoint(sketch, "E129.38.start.orphan", {"position": v(-43.13, -66.19) * mm});
            skPoint(sketch, "E129.40.end.orphan", {"position": v(-50.86, -70.38) * mm});
            skPoint(sketch, "E129.39.start.orphan", {"position": v(-50.86, -82.5) * mm});
            skPoint(sketch, "E129.42.end.orphan", {"position": v(-55.86, -82.5) * mm});
            skPoint(sketch, "E129.43.start.orphan", {"position": v(-55.86, -65.86) * mm});
            skPoint(sketch, "E129.45.start.orphan", {"position": v(-65.86, -55.86) * mm});
            skPoint(sketch, "E129.44.start.orphan", {"position": v(-82.5, -55.86) * mm});
            skPoint(sketch, "E129.47.start.orphan", {"position": v(-82.5, -50.86) * mm});
            skPoint(sketch, "E129.48.end.orphan", {"position": v(-66.19, -43.13) * mm});
            skPoint(sketch, "E129.48.start.orphan", {"position": v(-70.38, -50.86) * mm});
            skLineSegment(sketch, "E130", {"start": v(-75.68, 75.68) * mm, "end": v(0, 0) * mm, "construction": true});
            skLineSegment(sketch, "E131", {"start": v(0, 0) * mm, "end": v(75.68, -75.68) * mm, "construction": true});
            skLineSegment(sketch, "E132", {"start": v(-75.68, -75.68) * mm, "end": v(0, 0) * mm, "construction": true});
            skLineSegment(sketch, "E133", {"start": v(0, 0) * mm, "end": v(75.68, 75.68) * mm, "construction": true});
            skSolve(sketch);
        }
        {
            var Q0;
            Q0 = qSketchRegion(id + "F5", true);
            extrude(context, id + "F6", {"entities" : qUnion([Q0]), "operationType" : NewBodyOperationType.ADD, "depth" : 15.5 * mm, "offsetDistance" : 25 * mm});
        }
    });
